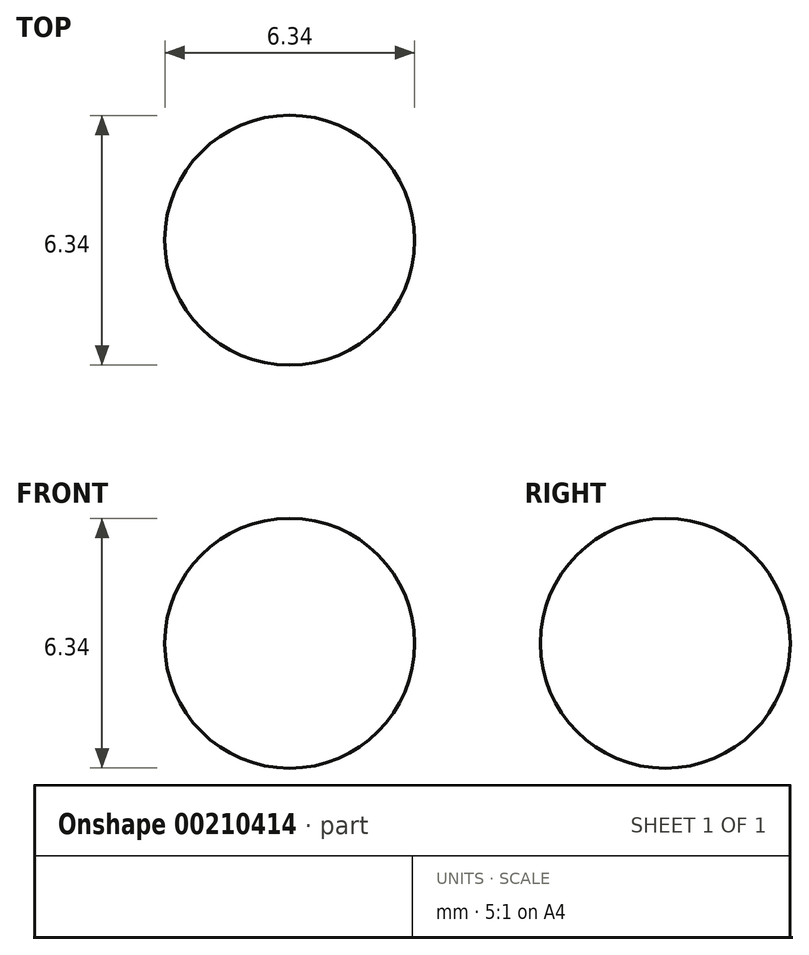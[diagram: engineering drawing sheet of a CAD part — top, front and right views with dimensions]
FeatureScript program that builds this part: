
annotation { "Feature Type Name" : "Feature", "Feature Type Description" : "" }
export const myFeature = defineFeature(function(context is Context, id is Id, definition is map)
    precondition{}
    {
        {
            var Q0;
            Q0=qCreatedBy(makeId("Front.planeOp"),FACE);
            var sketch = newSketch(context, id + "F0", { "sketchPlane" : qUnion([Q0])});
            skLineSegment(sketch, "E0", {"start": v(0, 0) * mm, "end": v(3.18, 0) * mm});
            skLineSegment(sketch, "E1", {"start": v(0, 0) * mm, "end": v(-3.18, 0) * mm});
            skArc(sketch, "E2", {"start": v(3.18, 0) * mm, "mid": v(0, 3.18) * mm, "end": v(-3.18, 0) * mm});
            skSolve(sketch);
        }
        {
            var Q0;
            Q0=makeQuery(id+"F0.imprint","IMPRINT",FACE,{"disambiguationData":[TD([[makeQuery(id+"F0.imprint","IMPRINT",EDGE,{"derivedFrom":sQuery(id+"F0.wireOp",EDGE,"E0")}),1.0]])]});
            var Q1;
            Q1=sQuery(id+"F0.wireOp",EDGE,"E1");
            revolve(context, id + "F1", {"entities" : qUnion([Q0]), "axis" : qUnion([Q1]), "revolveType" : RevolveType.FULL});
        }
    });
